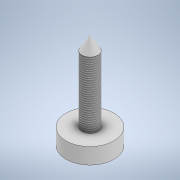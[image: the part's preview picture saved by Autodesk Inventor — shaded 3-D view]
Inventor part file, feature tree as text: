
AUTODESK INVENTOR PART (.ipt)
format: ipt  version: 2021.1 (Build 251245000, 245)  size: 110,592 bytes
history: native  units: in
note: dims shown in document units (in); Inventor stores cm internally (conversion verified against a paired STEP export)
features: revolve x1, thread x1, sketch x1
ambient origin geometry x8: Origin, YZ Plane, XZ Plane, XY Plane, X Axis, Y Axis, Z Axis, Center Point
bodies: Solid1 (feature_tree)
feature tree (3):
  revolve  "Revolution1"  [1 undecoded]
  thread  "Thread1"  [1 undecoded]
  sketch  "Sketch1"  dims[d0=6.0in d1=0.0in d2=1.0in d5=30.0deg d7=0.5in d9=90.0deg d10=4.134in d11=0.0in]
note: 2 required parameter values undecoded (feature->parameter linkage not recoverable at this tier; creation-order binding heuristic only, values carry confidence <= 0.55)